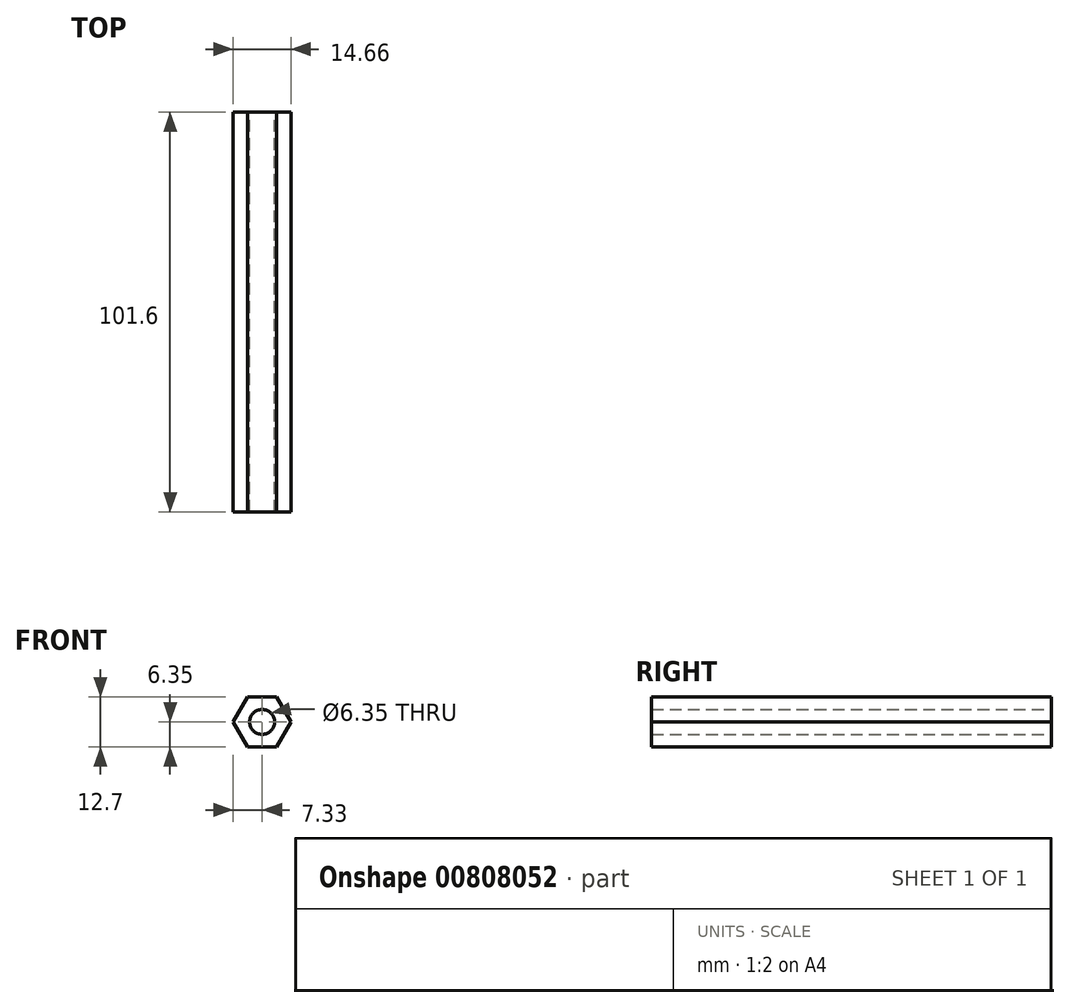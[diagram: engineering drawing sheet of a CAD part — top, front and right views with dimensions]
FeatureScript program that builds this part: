
annotation { "Feature Type Name" : "Feature", "Feature Type Description" : "" }
export const myFeature = defineFeature(function(context is Context, id is Id, definition is map)
    precondition{}
    {
        {
            var Q0;
            Q0=qCreatedBy(makeId("Front.planeOp"),FACE);
            var sketch = newSketch(context, id + "F0", { "sketchPlane" : qUnion([Q0])});
            skCircle(sketch, "E0", {"center": v(0, 0) * mm, "radius": 7.33 * mm, "construction": true});
            skLineSegment(sketch, "E1", {"start": v(-3.67, 6.35) * mm, "end": v(3.67, 6.35) * mm});
            skLineSegment(sketch, "E2", {"start": v(3.67, 6.35) * mm, "end": v(7.33, 0) * mm});
            skLineSegment(sketch, "E3", {"start": v(-3.67, 6.35) * mm, "end": v(-7.33, 0) * mm});
            skLineSegment(sketch, "E4", {"start": v(-7.33, 0) * mm, "end": v(-3.67, -6.35) * mm});
            skLineSegment(sketch, "E5", {"start": v(-3.67, -6.35) * mm, "end": v(3.67, -6.35) * mm});
            skLineSegment(sketch, "E6", {"start": v(3.67, -6.35) * mm, "end": v(7.33, 0) * mm});
            skCircle(sketch, "E7", {"center": v(0, 0) * mm, "radius": 3.18 * mm});
            skSolve(sketch);
        }
        {
            var Q0;
            Q0 = qSketchRegion(id + "F0", true);
            extrude(context, id + "F1", {"entities" : qUnion([Q0]), "endBound" : BoundingType.SYMMETRIC, "depth" : 101.6 * mm, "offsetDistance" : 25.4 * mm});
        }
        {
            var Q0;
            Q0=makeQuery(id+"F1.opExtrude","CAP_FACE",FACE,{"disambiguationData":[OSD([sQuery(id+"F0.wireOp",EDGE,"E1"),sQuery(id+"F0.wireOp",EDGE,"E2"),sQuery(id+"F0.wireOp",EDGE,"E3"),sQuery(id+"F0.wireOp",EDGE,"E4"),sQuery(id+"F0.wireOp",EDGE,"E5"),sQuery(id+"F0.wireOp",EDGE,"E6")])],"isStart":false});
            var sketch = newSketch(context, id + "F2", { "sketchPlane" : qUnion([Q0])});
            skCircle(sketch, "E8", {"center": v(0, 0) * mm, "radius": 13.9 * mm});
            skCircle(sketch, "E9", {"center": v(0, 0) * mm, "radius": 6.88 * mm});
            skSolve(sketch);
        }
        {
            var Q0;
            Q0=makeQuery(id+"F2.imprint","IMPRINT",FACE,{"disambiguationData":[TD([[makeQuery(id+"F2.imprint","IMPRINT",EDGE,{"derivedFrom":sQuery(id+"F2.wireOp",EDGE,"E8")}),1.0]])]});
            extrude(context, id + "F3", {"entities" : qUnion([Q0]), "operationType" : NewBodyOperationType.REMOVE, "endBound" : BoundingType.THROUGH_ALL, "oppositeDirection" : true, "depth" : 152.4 * mm, "offsetDistance" : 25.4 * mm});
        }
    });
